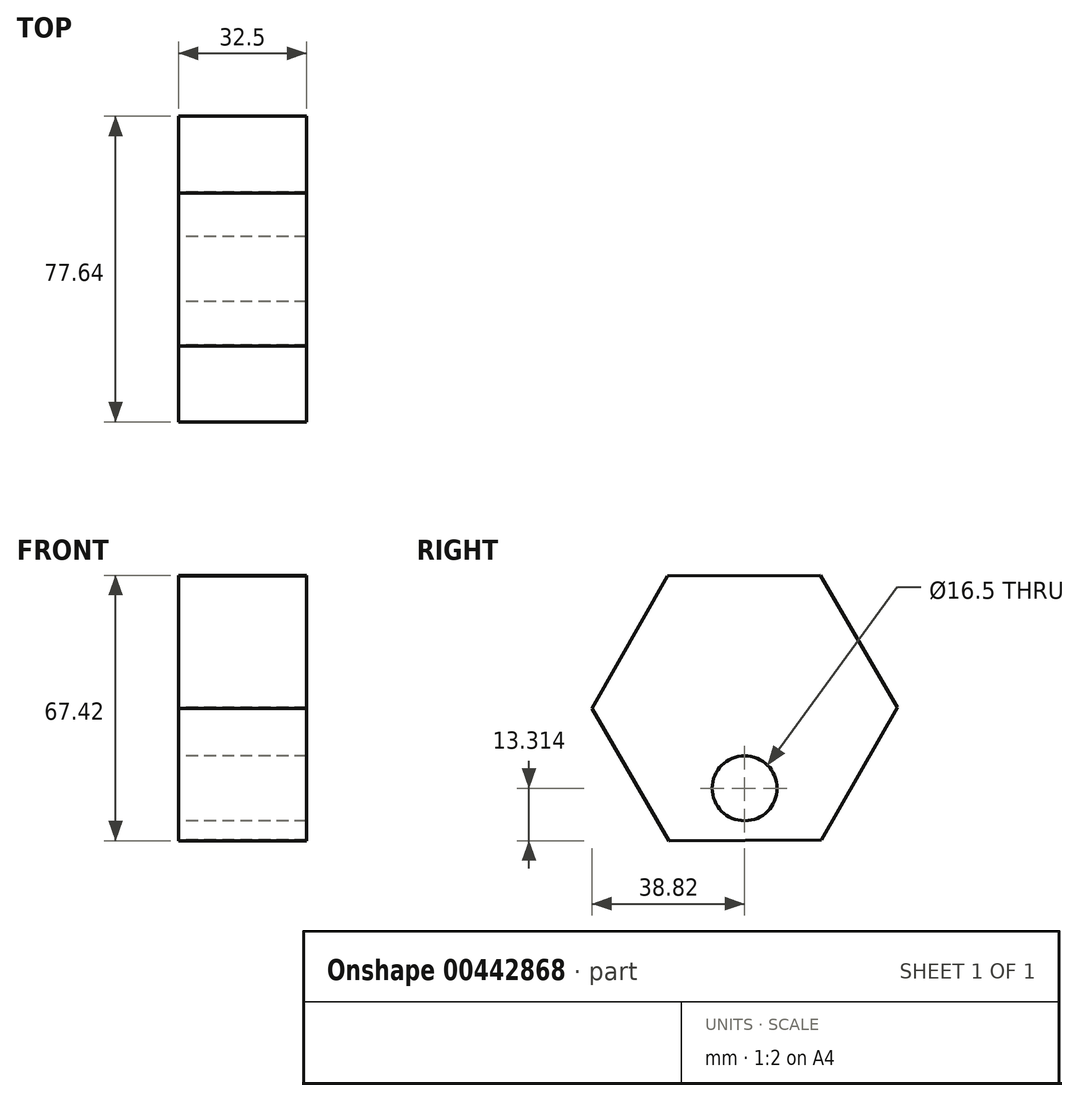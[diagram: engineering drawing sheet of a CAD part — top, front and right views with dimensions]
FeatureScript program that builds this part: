
annotation { "Feature Type Name" : "Feature", "Feature Type Description" : "" }
export const myFeature = defineFeature(function(context is Context, id is Id, definition is map)
    precondition{}
    {
        {
            var Q0;
            Q0=qCreatedBy(makeId("Right.planeOp"),FACE);
            var sketch = newSketch(context, id + "F0", { "sketchPlane" : qUnion([Q0])});
            skCircle(sketch, "E0.cCircle", {"center": v(0, 0) * mm, "radius": 38.82 * mm, "construction": true});
            skLineSegment(sketch, "E0.0", {"start": v(19.26, 33.7) * mm, "end": v(38.82, 0.17) * mm});
            skLineSegment(sketch, "E0.1", {"start": v(38.82, 0.17) * mm, "end": v(19.56, -33.54) * mm});
            skLineSegment(sketch, "E0.2", {"start": v(19.56, -33.54) * mm, "end": v(-19.26, -33.7) * mm});
            skLineSegment(sketch, "E0.3", {"start": v(-19.26, -33.7) * mm, "end": v(-38.82, -0.17) * mm});
            skLineSegment(sketch, "E0.4", {"start": v(-38.82, -0.17) * mm, "end": v(-19.56, 33.54) * mm});
            skLineSegment(sketch, "E0.5", {"start": v(-19.56, 33.54) * mm, "end": v(19.26, 33.7) * mm});
            skCircle(sketch, "E1", {"center": v(0, -20.4) * mm, "radius": 8.25 * mm});
            skSolve(sketch);
        }
        {
            var Q0;
            Q0 = qSketchRegion(id + "F0", true);
            extrude(context, id + "F1", {"entities" : qUnion([Q0]), "depth" : 32.5 * mm});
        }
    });
